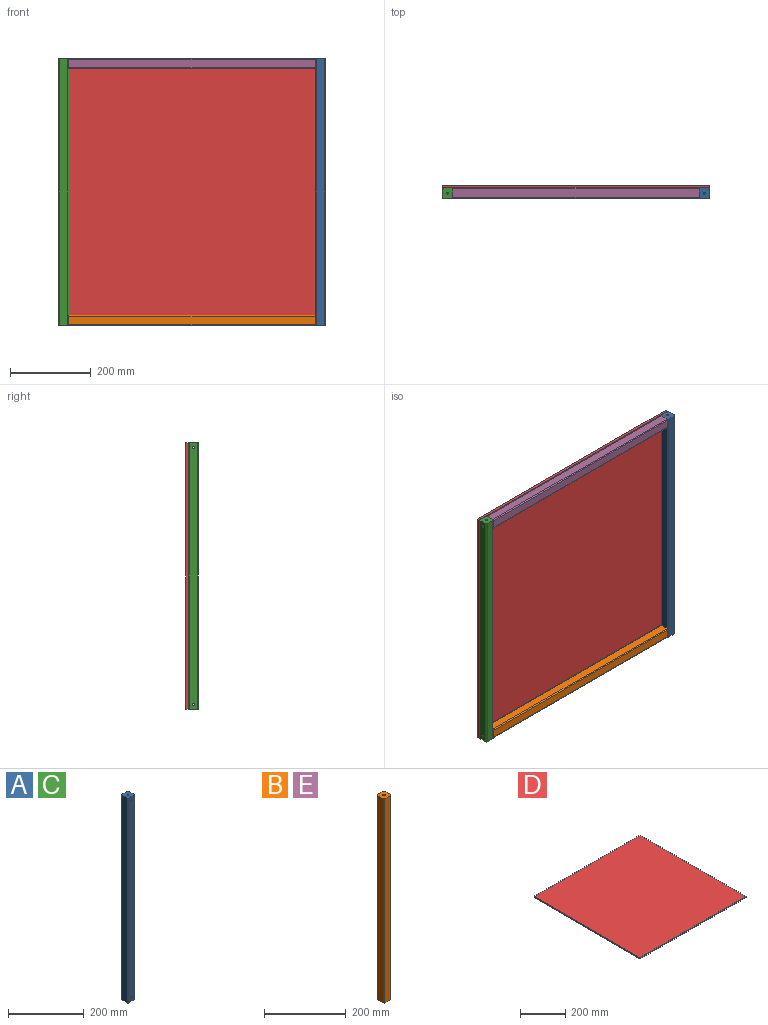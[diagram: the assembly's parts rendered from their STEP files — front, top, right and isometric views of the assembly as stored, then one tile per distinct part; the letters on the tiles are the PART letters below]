
ASSEMBLY  parts=5 mates=4
PART A: 17 faces, bbox 25.4x25.4x660.4 mm
  f0: cylinder r=2.54mm len=12.7mm, axis (0,0,-1), area 176.9mm2, adj f10,f12,f14
  f1: plane 660.4x20.32mm, normal (-1,0,0), area 13419.3mm2, adj f2,f9,f10,f11
  f2: cylinder r=2.54mm len=660.4mm, axis (0,0,-1), area 2634.9mm2, adj f1,f3,f10,f11
  f3: plane 660.4x20.32mm, normal (0,-1,0), area 13378.8mm2, adj f2,f4,f10,f11,f14,f16
  f4: cylinder r=2.54mm len=660.4mm, axis (0,0,-1), area 2634.9mm2, adj f3,f5,f10,f11
  f5: plane 660.4x20.32mm, normal (1,0,0), area 13419.3mm2, adj f4,f6,f10,f11
  f6: cylinder r=2.54mm len=660.4mm, axis (0,0,-1), area 2634.9mm2, adj f5,f7,f10,f11
  f7: plane 660.4x20.32mm, normal (0,1,0), area 13378.8mm2, adj f6,f9,f10,f11,f12,f15
  f8: cylinder r=2.54mm len=12.7mm, axis (0,0,-1), area 176.9mm2, adj f11,f15,f16
  f9: cylinder r=2.54mm len=660.4mm, axis (0,0,-1), area 2634.9mm2, adj f1,f7,f10,f11
  f10: plane 25.4x25.4mm, normal (0,0,1), area 619.4mm2, adj f0,f1,f2,f3,f4,f5,f6,f7
  f11: plane 25.4x25.4mm, normal (0,0,-1), area 619.4mm2, adj f1,f2,f3,f4,f5,f6,f7,f8
  f12: cylinder r=2.54mm len=12.7mm, axis (0,-1,0), area 176.9mm2, adj f0,f7,f13
  f13: cylinder r=2.54mm len=635mm, axis (0,0,-1), area 10082.5mm2, adj f12,f14,f15,f16
  f14: cylinder r=2.54mm len=12.7mm, axis (0,-1,0), area 176.9mm2, adj f0,f3,f13
  f15: cylinder r=2.54mm len=12.7mm, axis (0,-1,0), area 176.9mm2, adj f7,f8,f13
  f16: cylinder r=2.54mm len=12.7mm, axis (0,-1,0), area 176.9mm2, adj f3,f8,f13
PART B: 11 faces, bbox 25.4x25.4x609.6 mm
  f0: plane 609.6x20.32mm, normal (-1,0,0), area 12387.1mm2, adj f1,f8,f9,f10
  f1: cylinder r=2.54mm len=609.6mm, axis (0,0,-1), area 2432.2mm2, adj f0,f2,f9,f10
  f2: plane 609.6x20.32mm, normal (0,-1,0), area 12387.1mm2, adj f1,f3,f9,f10
  f3: cylinder r=2.54mm len=609.6mm, axis (0,0,-1), area 2432.2mm2, adj f2,f4,f9,f10
  f4: plane 609.6x20.32mm, normal (1,0,0), area 12387.1mm2, adj f3,f5,f9,f10
  f5: cylinder r=2.54mm len=609.6mm, axis (0,0,-1), area 2432.2mm2, adj f4,f6,f9,f10
  f6: plane 609.6x20.32mm, normal (0,1,0), area 12387.1mm2, adj f5,f8,f9,f10
  f7: cylinder r=2.54mm len=609.6mm, axis (0,0,-1), area 9728.8mm2, adj f9,f10
  f8: cylinder r=2.54mm len=609.6mm, axis (0,0,-1), area 2432.2mm2, adj f0,f6,f9,f10
  f9: plane 25.4x25.4mm, normal (0,0,1), area 619.4mm2, adj f0,f1,f2,f3,f4,f5,f6,f7
  f10: plane 25.4x25.4mm, normal (0,0,-1), area 619.4mm2, adj f0,f1,f2,f3,f4,f5,f6,f7
PART C: same geometry as A
PART D: 6 faces, bbox 660.4x660.4x6.4 mm
  f0: plane 660.4x6.35mm, normal (0,-1,0), area 4193.5mm2, adj f1,f3,f4,f5
  f1: plane 660.4x6.35mm, normal (1,0,0), area 4193.5mm2, adj f0,f2,f4,f5
  f2: plane 660.4x6.35mm, normal (0,1,0), area 4193.5mm2, adj f1,f3,f4,f5
  f3: plane 660.4x6.35mm, normal (-1,0,0), area 4193.5mm2, adj f0,f2,f4,f5
  f4: plane 660.4x660.4mm, normal (0,0,1), area 436128.2mm2, adj f0,f1,f2,f3
  f5: plane 660.4x660.4mm, normal (0,0,-1), area 436128.2mm2, adj f0,f1,f2,f3
PART E: same geometry as B
PLACE A rot(axis=(0,0,-1),90deg) t=(366.05,-159.31,51.78)mm
PLACE B rot(axis=(0,1,0),90deg) t=(-95.11,-367.98,118.47)mm
PLACE C rot(axis=(0,0,1),90deg) t=(53.32,-187.43,51.78)mm
PLACE D rot(axis=(1,0,0),90deg) t=(-205.83,-154.32,772.39)mm
PLACE E rot(axis=(0,1,0),90deg) t=(-95.11,-367.98,753.47)mm
MATE fastened B.f7 <-> C.f15  axis (-1,0,0) through (-95.11,-173.37,64.48)mm
MATE fastened D.f4 <-> E.f6  axis (0,-1,0) through (209.69,-160.67,712.18)mm
MATE fastened C.f12 <-> E.f7  axis (1,0,0) through (-95.11,-173.37,699.48)mm
MATE fastened A.f12 <-> E.f7  axis (-1,0,0) through (514.49,-173.37,699.48)mm
